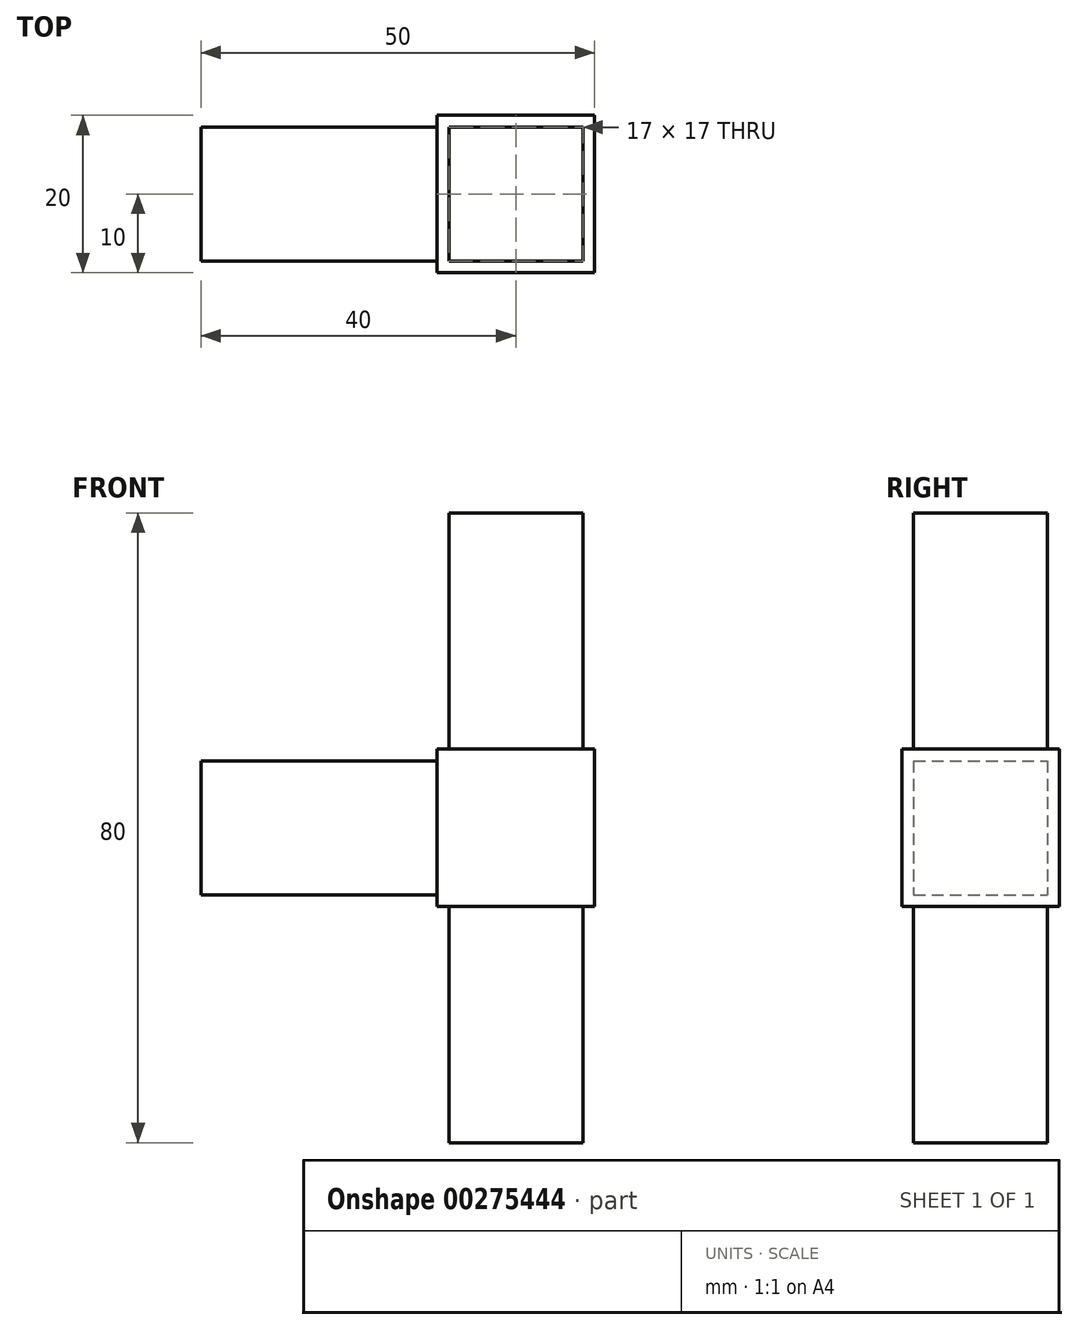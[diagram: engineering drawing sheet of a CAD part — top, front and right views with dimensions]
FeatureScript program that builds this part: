
annotation { "Feature Type Name" : "Feature", "Feature Type Description" : "" }
export const myFeature = defineFeature(function(context is Context, id is Id, definition is map)
    precondition{}
    {
        {
            var Q0;
            Q0=qCreatedBy(makeId("Top.planeOp"),FACE);
            var sketch = newSketch(context, id + "F0", { "sketchPlane" : qUnion([Q0])});
            skLineSegment(sketch, "E0.bottom", {"start": v(10, -10) * mm, "end": v(-10, -10) * mm});
            skLineSegment(sketch, "E0.top", {"start": v(10, 10) * mm, "end": v(-10, 10) * mm});
            skLineSegment(sketch, "E0.left", {"start": v(10, -10) * mm, "end": v(10, 10) * mm});
            skLineSegment(sketch, "E0.right", {"start": v(-10, -10) * mm, "end": v(-10, 10) * mm});
            skPoint(sketch, "E0.middle", {"position": v(0, 0) * mm});
            skLineSegment(sketch, "E1", {"start": v(0, -10) * mm, "end": v(8.5, -10) * mm});
            skLineSegment(sketch, "E2.bottom", {"start": v(8.5, -10) * mm, "end": v(-8.5, -10) * mm});
            skLineSegment(sketch, "E2.top", {"start": v(8.5, -40) * mm, "end": v(-8.5, -40) * mm});
            skLineSegment(sketch, "E2.left", {"start": v(8.5, -10) * mm, "end": v(8.5, -40) * mm});
            skLineSegment(sketch, "E2.right", {"start": v(-8.5, -10) * mm, "end": v(-8.5, -40) * mm});
            skLineSegment(sketch, "E3", {"start": v(-10, 0) * mm, "end": v(-10, -8.5) * mm});
            skLineSegment(sketch, "E4.bottom", {"start": v(-10, -8.5) * mm, "end": v(-40, -8.5) * mm});
            skLineSegment(sketch, "E4.top", {"start": v(-10, 8.5) * mm, "end": v(-40, 8.5) * mm});
            skLineSegment(sketch, "E4.left", {"start": v(-10, -8.5) * mm, "end": v(-10, 8.5) * mm});
            skLineSegment(sketch, "E4.right", {"start": v(-40, -8.5) * mm, "end": v(-40, 8.5) * mm});
            skSolve(sketch);
        }
        {
            var Q0;
            {var subQ1=sQuery(id+"F0.wireOp",EDGE,"E0.top");Q0=makeQuery(id+"F0.imprint","IMPRINT",FACE,{"disambiguationData":[TD([[makeQuery(id+"F0.imprint","IMPRINT",EDGE,{"derivedFrom":subQ1}),1.0]])]});}
            extrude(context, id + "F1", {"entities" : qUnion([Q0]), "depth" : 20 * mm});
        }
        {
            var Q0;
            {var subQ4=sQuery(id+"F0.wireOp",EDGE,"E4.bottom");Q0=makeQuery(id+"F0.imprint","IMPRINT",FACE,{"disambiguationData":[TD([[makeQuery(id+"F0.imprint","IMPRINT",EDGE,{"derivedFrom":subQ4}),-1.0]])]});}
            extrude(context, id + "F2", {"entities" : qUnion([Q0]), "operationType" : NewBodyOperationType.ADD, "depth" : 18.5 * mm, "hasSecondDirection" : true, "secondDirectionOppositeDirection" : false, "secondDirectionDepth" : 1.5 * mm});
        }
        {
            var Q0;
            Q0=makeQuery(id+"F1.opExtrude","CAP_FACE",FACE,{"disambiguationData":[OSD([sQuery(id+"F0.wireOp",EDGE,"E0.bottom"),sQuery(id+"F0.wireOp",EDGE,"E0.top"),sQuery(id+"F0.wireOp",EDGE,"E0.left"),sQuery(id+"F0.wireOp",EDGE,"E0.right"),sQuery(id+"F0.wireOp",EDGE,"E2.bottom"),sQuery(id+"F0.wireOp",EDGE,"E4.left")])],"isStart":false});
            var sketch = newSketch(context, id + "F3", { "sketchPlane" : qUnion([Q0])});
            skLineSegment(sketch, "E5.bottom", {"start": v(8.5, -8.5) * mm, "end": v(-8.5, -8.5) * mm});
            skLineSegment(sketch, "E5.top", {"start": v(8.5, 8.5) * mm, "end": v(-8.5, 8.5) * mm});
            skLineSegment(sketch, "E5.left", {"start": v(8.5, -8.5) * mm, "end": v(8.5, 8.5) * mm});
            skLineSegment(sketch, "E5.right", {"start": v(-8.5, -8.5) * mm, "end": v(-8.5, 8.5) * mm});
            skPoint(sketch, "E5.middle", {"position": v(0, 0) * mm});
            skSolve(sketch);
        }
        {
            var Q0;
            Q0=qSketchRegion(id+"F3",true);
            extrude(context, id + "F4", {"entities" : qUnion([Q0]), "operationType" : NewBodyOperationType.ADD, "depth" : 30 * mm});
        }
        {
            var Q0;
            Q0=makeQuery(id+"F1.opExtrude","CAP_FACE",FACE,{"disambiguationData":[OSD([sQuery(id+"F0.wireOp",EDGE,"E0.bottom"),sQuery(id+"F0.wireOp",EDGE,"E0.top"),sQuery(id+"F0.wireOp",EDGE,"E0.left"),sQuery(id+"F0.wireOp",EDGE,"E0.right"),sQuery(id+"F0.wireOp",EDGE,"E2.bottom"),sQuery(id+"F0.wireOp",EDGE,"E4.left")])],"isStart":true});
            var sketch = newSketch(context, id + "F5", { "sketchPlane" : qUnion([Q0])});
            skLineSegment(sketch, "E6.bottom", {"start": v(8.5, -8.5) * mm, "end": v(-8.5, -8.5) * mm});
            skLineSegment(sketch, "E6.top", {"start": v(8.5, 8.5) * mm, "end": v(-8.5, 8.5) * mm});
            skLineSegment(sketch, "E6.left", {"start": v(8.5, -8.5) * mm, "end": v(8.5, 8.5) * mm});
            skLineSegment(sketch, "E6.right", {"start": v(-8.5, -8.5) * mm, "end": v(-8.5, 8.5) * mm});
            skPoint(sketch, "E6.middle", {"position": v(0, 0) * mm});
            skSolve(sketch);
        }
        {
            var Q0;
            Q0=qSketchRegion(id+"F5",true);
            extrude(context, id + "F6", {"entities" : qUnion([Q0]), "operationType" : NewBodyOperationType.ADD, "depth" : 30 * mm});
        }
    });
